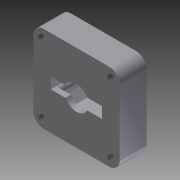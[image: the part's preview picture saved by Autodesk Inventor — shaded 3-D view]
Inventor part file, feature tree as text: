
AUTODESK INVENTOR PART (.ipt)
format: ipt  version: 2012 (Build 160160000, 160)  size: 173,056 bytes
history: native  units: in
note: dims shown in document units (in); Inventor stores cm internally (conversion verified against a paired STEP export)
features: thread x4, extrude x2, fillet x2, hole x2, sketch x1
ambient origin geometry x8: Origin, YZ Plane, XZ Plane, XY Plane, X Axis, Y Axis, Z Axis, Center Point
bodies: Solid1 (feature_tree)
feature tree (11):
  sketch  "Sketch1"  dims[d0=0.9449in d1=0.4724in d2=1.0236in d3=0.5118in d4=0.0787in d5=0.2559in d6=0.128in d7=0.0787in d8=0.5625in d9=2.0in d10=1.0in d11=2.0in d12=1.0in d13=0.1181in d14=0.3937in d15=0.1575in d16=0.1575in d17=0.1575in d18=0.1575in d19=0.1575in d20=0.2in d21=0.2in d22=0.2in d23=0.2in d24=0.5in d25=0.0in d26=0.125in d27=0.164in d28=0.75in d29=0.27in d30=0.2in d31=0.5635in d32=1.0in d33=0.8108in d34=1.6in d35=1.6in d36=1.0in d37=0.0in d38=1.0in d39=0.0in d40=1.0in d41=0.0in d42=1.0in d43=0.0in d44=0.125in d45=0.0in d46=0.164in d47=0.75in d48=0.375in d49=0.25in d50=0.5635in d51=1.0in d52=0.8108in d53=0.25in]
  extrude  "Extrusion1"  Depth=0.4724in
  fillet  "Fillet1"  Radius=1.0236in
  extrude  "Extrusion2"  Depth=0.5118in
  hole  "Hole1"  [1 undecoded]
  thread  "Thread1"  [1 undecoded]
  thread  "Thread2"  [1 undecoded]
  thread  "Thread3"  [1 undecoded]
  thread  "Thread4"  [1 undecoded]
  hole  "Hole2"  [1 undecoded]
  fillet  "Fillet2"  Radius=1.0in
note: 6 required parameter values undecoded (feature->parameter linkage not recoverable at this tier; creation-order binding heuristic only, values carry confidence <= 0.55)
